# Revit family: Door-Hardware_Accessories_Hager_Exit-Switch
name_source: partatom
category: Specialty Equipment
units: mm (PartAtom-declared; Revit-internal decimal feet)

## family parameters
Always vertical = No
Classification Number = 23.30.40.00
Cut with Voids When Loaded = No
Enable Cutting in Views = No
Maintain Annotation Orientation = No
Part Type = Normal
Room Calculation Point = No
Round Connector Dimension = Use Diameter
Shared = Yes
Work Plane-Based = Yes

## types (5) — shared parameters
Assembly Code = C1020410
Capacity = as Specified
Default Elevation = 0' - 0"
Keynote = 087100
Manufacturer = Hager Companies
Manufacturer Fax = 800-782-0149
Manufacturer Website = http://www.hagerco.com
Product Data = http://www.arcat.com
Revision = R1_2015-10
Sales Information = http://www.hagerco.com
Specification = http://www.arcat.com
URL = http://www.hagerco.com
zero-valued in all types: Expected Lifespan (Years), Maintenance Schedule (Months), Warranty Duration (Years)

## per-type parameters (varying)
| type | Description | Model | Operating Temperature Range | Rectangle Button | Rectangle and Round Button | Round Button | Standards Conformance |
| 2978 Touchless | Hager Touchless Exit Switch - 2978 as Specified | 2978 | -20 to 120 F | No | Yes | No | Sanitary Entry and Exit  ;  4in Sensor Range |
| 2977 Piezoelectric | Hager Piezoelectric Exit Switch - 2977 as Specified | 2977 | -40 to 120 F | No | No | Yes | Vandal Resistant  ;  Weatherized |
| 2973 Fixed Timer | Hager Fixed Timer Exit Switch - 2973-IFT as Specified | 2973-IFT | -20 to 120 F | Yes | No | No | NFPA  ;  IBC  ;  IFC  ;  California Fire Code |
| 2972 Adjustable Timer | Hager Adjustable Timer Exit Switch - 2972-IET as Specified | 2972-IET | -20 to 120 F | Yes | No | No | NFPA  ;  ADA with proper options |
| 2972 Momentary | Hager Momentary Exit Switch - 2972-MSD as Specified | 2972-MSD | -20 to 120 F | Yes | No | No | NFPA  ;  ADA with proper options |

## geometry (parser evidence)
native form markers: Blend x6, Sweep x2
no freeform markers — native parametric forms only
